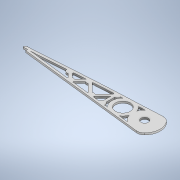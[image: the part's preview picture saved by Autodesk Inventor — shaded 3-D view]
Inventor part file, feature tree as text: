
AUTODESK INVENTOR PART (.ipt)
format: ipt  version: 2022 (Build 260153000, 153)  size: 355,328 bytes
history: native  units: mm
features: extrude x1, sketch x1
ambient origin geometry x8: Origin, YZ Plane, XZ Plane, XY Plane, X Axis, Y Axis, Z Axis, Center Point
bodies: Body1 (feature_tree)
feature tree (2):
  extrude  "Extrusion5"  Depth=10.0mm
  sketch  "Sketch1"  dims[d31=34.456mm d50=368.759386mm d57=16.0mm d69=8.0mm d70=23.0mm d71=8.0mm d73=16.0mm d80=19.0mm d81=16.0mm d82=1.0mm d83=1.0mm d84=1.0mm d85=1.0mm d86=1.0mm d87=0.8mm d88=1.0mm d90=19.0mm d94=5.0mm d95=5.0mm d105=5.0mm d106=5.0mm d108=2.0mm d109=19.0mm d114=5.0mm d115=5.0mm d116=24.0mm d117=2.5mm d118=2.5mm d123=2.5mm d124=2.5mm d125=10.0mm d126=24.0mm d127=24.0mm d128=27.0mm d135=0.5mm d136=45.0deg d139=7.0mm d165=45.0deg d169=27.0mm d175=90.0deg d181=45.0deg d185=7.0mm d186=45.0deg d190=7.0mm d191=45.0deg d197=90.0deg d203=90.0deg d206=7.0mm d207=2.0mm d208=0.0mm]
